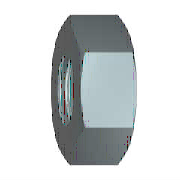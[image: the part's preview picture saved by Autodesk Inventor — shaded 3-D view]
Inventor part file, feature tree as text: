
AUTODESK INVENTOR PART (.ipt)
format: ipt  version: 2024 (Build 280153000, 153)  size: 181,760 bytes
history: native  units: mm (DEFAULTED — no unit token found)
features: other x3, extrude x1, chamfer x1, hole x1, plane x1
ambient origin geometry x7: Origin, YZ Plane, XZ Plane, X Axis, Y Axis, Z Axis, Center Point
bodies: Solid1 (feature_tree)
feature tree (7):
  extrude  "Cuerpo"  Depth=3.695042mm
  chamfer  "Chaflán1"  Distance=1.3mm
  hole  "Rosca"  [1 undecoded]
  other  "Work Axis1"
  plane  "Work Plane1"
  other  "Edición directa1"
  other  "Escala1"
note: 1 required parameter value undecoded (feature->parameter linkage not recoverable at this tier; creation-order binding heuristic only, values carry confidence <= 0.55)
